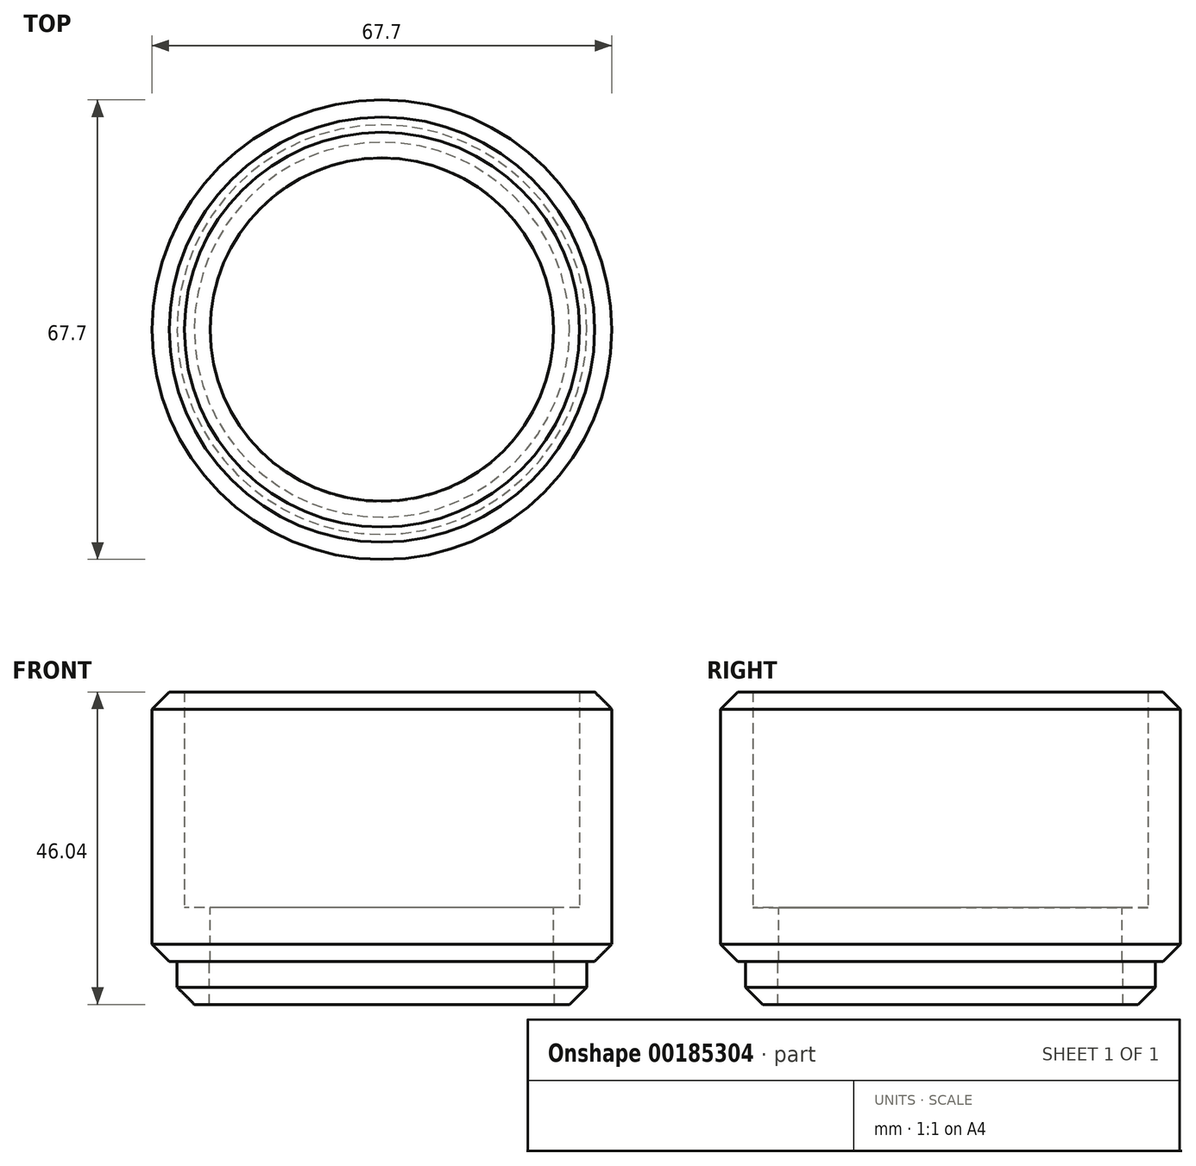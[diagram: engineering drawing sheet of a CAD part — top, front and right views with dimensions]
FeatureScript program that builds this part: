
annotation { "Feature Type Name" : "Feature", "Feature Type Description" : "" }
export const myFeature = defineFeature(function(context is Context, id is Id, definition is map)
    precondition{}
    {
        {
            var Q0;
            Q0=qCreatedBy(makeId("Top.planeOp"),FACE);
            var sketch = newSketch(context, id + "F0", { "sketchPlane" : qUnion([Q0])});
            skCircle(sketch, "E0", {"center": v(0, 0) * mm, "radius": 29.08 * mm});
            skCircle(sketch, "E1.0", {"center": v(0, 0) * mm, "radius": 33.85 * mm});
            skCircle(sketch, "E2.0", {"center": v(0, 0) * mm, "radius": 25.27 * mm});
            skSolve(sketch);
        }
        {
            var Q0;
            Q0=makeQuery(id+"F0.imprint","IMPRINT",FACE,{"disambiguationData":[TD([[makeQuery(id+"F0.imprint","IMPRINT",EDGE,{"derivedFrom":sQuery(id+"F0.wireOp",EDGE,"E0")}),-1.0]])]});
            extrude(context, id + "F1", {"entities" : qUnion([Q0]), "depth" : 31.75 * mm});
        }
        {
            var Q0;
            Q0=makeQuery(id+"F0.imprint","IMPRINT",FACE,{"disambiguationData":[TD([[makeQuery(id+"F0.imprint","IMPRINT",EDGE,{"derivedFrom":sQuery(id+"F0.wireOp",EDGE,"E0")}),1.0]])]});
            var Q1;
            Q1=makeQuery(id+"F0.imprint","IMPRINT",FACE,{"disambiguationData":[TD([[makeQuery(id+"F0.imprint","IMPRINT",EDGE,{"derivedFrom":sQuery(id+"F0.wireOp",EDGE,"E0")}),-1.0]])]});
            extrude(context, id + "F2", {"entities" : qUnion([Q0, Q1]), "operationType" : NewBodyOperationType.ADD, "oppositeDirection" : true, "depth" : 7.94 * mm});
        }
        {
            var Q0;
            Q0=makeQuery(id+"F2.opExtrude","CAP_FACE",FACE,{"disambiguationData":[OSD([sQuery(id+"F0.wireOp",EDGE,"E1.0"),sQuery(id+"F0.wireOp",EDGE,"E2.0")])],"isStart":false});
            var sketch = newSketch(context, id + "F3", { "sketchPlane" : qUnion([Q0])});
            skCircle(sketch, "E3", {"center": v(0, 0) * mm, "radius": 25.4 * mm});
            skCircle(sketch, "E4.0", {"center": v(0, 0) * mm, "radius": 30.16 * mm});
            skSolve(sketch);
        }
        {
            var Q0;
            Q0 = qSketchRegion(id + "F3", true);
            extrude(context, id + "F4", {"entities" : qUnion([Q0]), "operationType" : NewBodyOperationType.ADD, "depth" : 6.35 * mm});
        }
        {
            var Q0;
            Q0=makeQuery(id+"F1.opExtrude","CAP_EDGE",EDGE,{"disambiguationData":[OSD([sQuery(id+"F0.wireOp",EDGE,"E1.0")])],"isStart":false});
            var Q1;
            Q1=makeQuery(id+"F2.opExtrude","CAP_EDGE",EDGE,{"disambiguationData":[OSD([sQuery(id+"F0.wireOp",EDGE,"E1.0")])],"isStart":false});
            var Q2;
            Q2=makeQuery(id+"F4.opExtrude","CAP_EDGE",EDGE,{"disambiguationData":[OSD([sQuery(id+"F3.wireOp",EDGE,"E4.0")])],"isStart":false});
            chamfer(context, id + "F5", {"entities" : qUnion([Q0, Q1, Q2]), "width" : 2.54 * mm, "tangentPropagation" : true});
        }
    });
